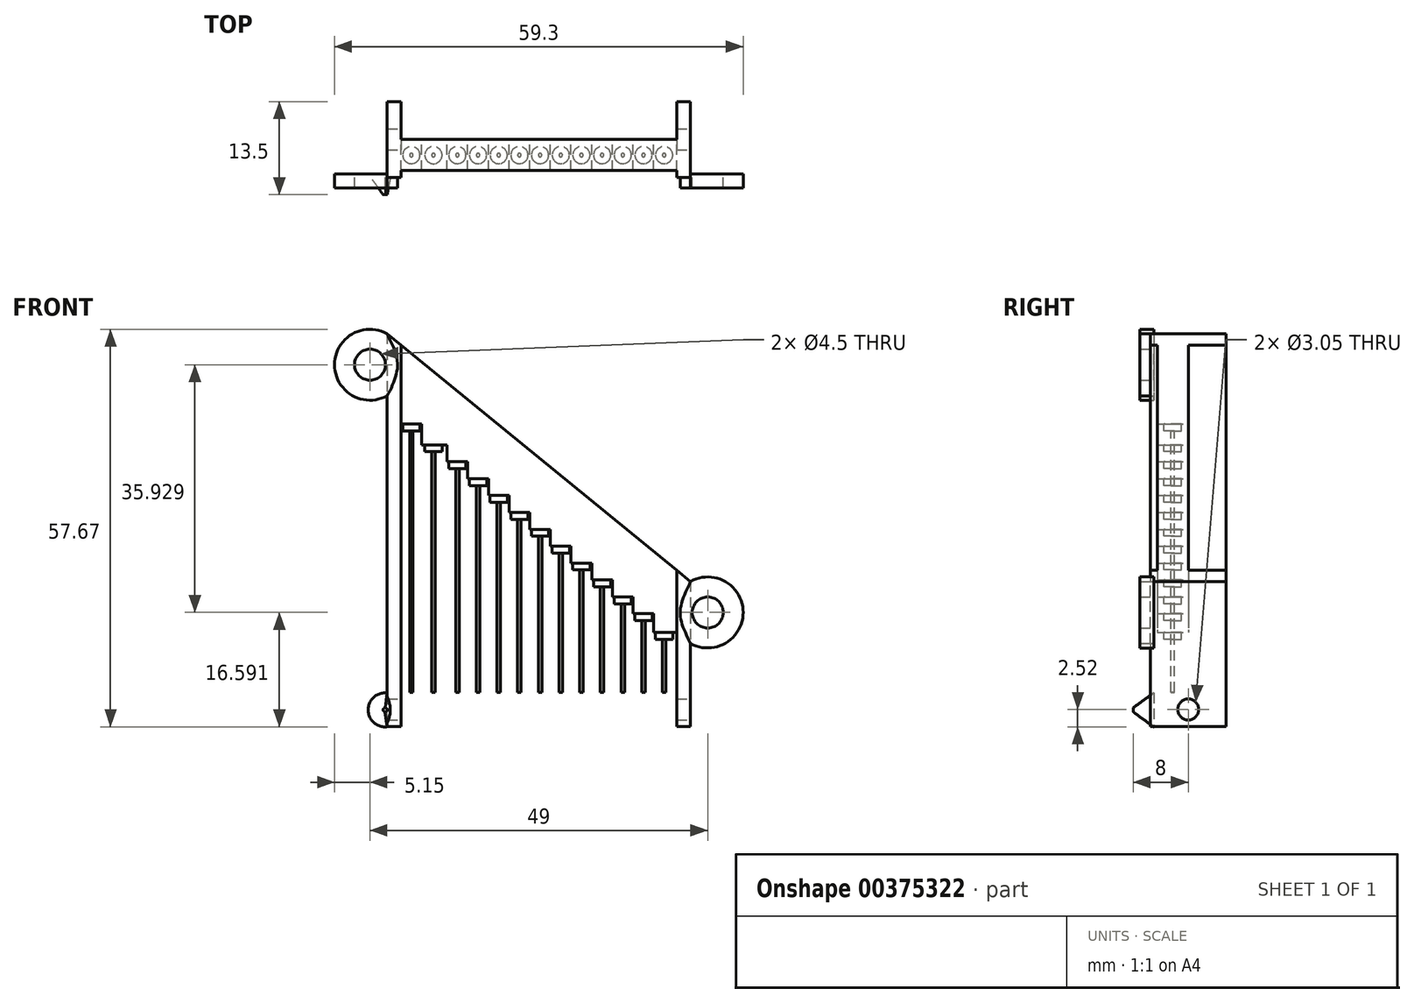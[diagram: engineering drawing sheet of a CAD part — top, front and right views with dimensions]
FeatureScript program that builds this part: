
annotation { "Feature Type Name" : "Feature", "Feature Type Description" : "" }
export const myFeature = defineFeature(function(context is Context, id is Id, definition is map)
    precondition{}
    {
        {
            var Q0;
            Q0=qCreatedBy(makeId("Front.planeOp"),FACE);
            var sketch = newSketch(context, id + "F0", { "sketchPlane" : qUnion([Q0])});
            skLineSegment(sketch, "E0.top", {"start": v(-22, -28.5) * mm, "end": v(22, -28.5) * mm});
            skLineSegment(sketch, "E0.left", {"start": v(-22, 28.5) * mm, "end": v(-22, -28.5) * mm});
            skPoint(sketch, "E0.middle", {"position": v(0, 0) * mm});
            skLineSegment(sketch, "E1", {"start": v(-22, 28.5) * mm, "end": v(22, -7.43) * mm});
            skPoint(sketch, "E2.orphan", {"position": v(22, 28.5) * mm});
            skLineSegment(sketch, "E3", {"start": v(22, -7.43) * mm, "end": v(22, -28.5) * mm});
            skLineSegment(sketch, "E4", {"start": v(22, -7.43) * mm, "end": v(-22, 28.5) * mm});
            skLineSegment(sketch, "E5", {"start": v(-20, -28.5) * mm, "end": v(-20, 26.87) * mm});
            skLineSegment(sketch, "E6", {"start": v(20, -5.8) * mm, "end": v(20, -28.5) * mm});
            skLineSegment(sketch, "E7", {"start": v(16.67, -12.12) * mm, "end": v(20, -14.83) * mm});
            skLineSegment(sketch, "E8", {"start": v(-20, 15.38) * mm, "end": v(-17, 15.38) * mm});
            skLineSegment(sketch, "E9", {"start": v(-17, 15.38) * mm, "end": v(-17, 12.38) * mm});
            skLineSegment(sketch, "E10", {"start": v(-17, 12.38) * mm, "end": v(-13.33, 12.38) * mm});
            skLineSegment(sketch, "E11", {"start": v(-13.33, 12.38) * mm, "end": v(-13.33, 9.93) * mm});
            skLineSegment(sketch, "E12", {"start": v(-13.33, 9.93) * mm, "end": v(-10.33, 9.93) * mm});
            skLineSegment(sketch, "E13", {"start": v(-10.33, 9.93) * mm, "end": v(-10.33, 7.48) * mm});
            skLineSegment(sketch, "E14", {"start": v(-10.33, 7.48) * mm, "end": v(-7.33, 7.48) * mm});
            skLineSegment(sketch, "E15", {"start": v(-7.33, 7.48) * mm, "end": v(-7.33, 5.03) * mm});
            skLineSegment(sketch, "E16", {"start": v(-7.33, 5.03) * mm, "end": v(-4.33, 5.03) * mm});
            skLineSegment(sketch, "E17", {"start": v(-4.33, 5.03) * mm, "end": v(-4.33, 2.58) * mm});
            skLineSegment(sketch, "E18", {"start": v(-4.33, 2.58) * mm, "end": v(-1.33, 2.58) * mm});
            skLineSegment(sketch, "E19", {"start": v(-1.33, 2.58) * mm, "end": v(-1.33, 0.13) * mm});
            skLineSegment(sketch, "E20", {"start": v(-1.33, 0.13) * mm, "end": v(1.67, 0.13) * mm});
            skLineSegment(sketch, "E21", {"start": v(1.67, 0.13) * mm, "end": v(1.67, -2.32) * mm});
            skLineSegment(sketch, "E22", {"start": v(1.67, -2.32) * mm, "end": v(4.67, -2.32) * mm});
            skLineSegment(sketch, "E23", {"start": v(4.67, -2.32) * mm, "end": v(4.67, -4.77) * mm});
            skLineSegment(sketch, "E24", {"start": v(4.67, -4.77) * mm, "end": v(7.67, -4.77) * mm});
            skLineSegment(sketch, "E25", {"start": v(7.67, -4.77) * mm, "end": v(7.67, -7.22) * mm});
            skLineSegment(sketch, "E26", {"start": v(7.67, -7.22) * mm, "end": v(10.67, -7.22) * mm});
            skLineSegment(sketch, "E27", {"start": v(10.67, -7.22) * mm, "end": v(10.67, -9.67) * mm});
            skLineSegment(sketch, "E28", {"start": v(10.67, -9.67) * mm, "end": v(13.67, -9.67) * mm});
            skLineSegment(sketch, "E29", {"start": v(13.67, -9.67) * mm, "end": v(13.67, -12.12) * mm});
            skLineSegment(sketch, "E30", {"start": v(13.67, -12.12) * mm, "end": v(16.67, -12.12) * mm});
            skLineSegment(sketch, "E31", {"start": v(16.67, -12.12) * mm, "end": v(16.67, -14.83) * mm});
            skLineSegment(sketch, "E32", {"start": v(16.67, -14.83) * mm, "end": v(20, -14.83) * mm});
            skSolve(sketch);
        }
        {
            var Q0;
            {var subQ0=sQuery(id+"F0.wireOp",EDGE,"E7");Q0=makeQuery(id+"F0.imprint","IMPRINT",FACE,{"disambiguationData":[TD([[makeQuery(id+"F0.imprint","IMPRINT",EDGE,{"derivedFrom":subQ0}),1.0]])]});}
            var Q1;
            Q1=makeQuery(id+"F0.imprint","IMPRINT",FACE,{"disambiguationData":[TD([[makeQuery(id+"F0.imprint","IMPRINT",EDGE,{"derivedFrom":sQuery(id+"F0.wireOp",EDGE,"E7")}),-1.0]])]});
            extrude(context, id + "F1", {"entities" : qUnion([Q0, Q1]), "depth" : 4.5 * mm});
        }
        {
            var Q0;
            {var subQ0=sQuery(id+"F0.wireOp",EDGE,"E0.left");Q0=makeQuery(id+"F0.imprint","IMPRINT",FACE,{"disambiguationData":[TD([[makeQuery(id+"F0.imprint","IMPRINT",EDGE,{"derivedFrom":subQ0}),1.0]])]});}
            var Q1;
            {var subQ0=sQuery(id+"F0.wireOp",EDGE,"E3");Q1=makeQuery(id+"F0.imprint","IMPRINT",FACE,{"disambiguationData":[TD([[makeQuery(id+"F0.imprint","IMPRINT",EDGE,{"derivedFrom":subQ0}),-1.0]])]});}
            extrude(context, id + "F2", {"entities" : qUnion([Q0, Q1]), "operationType" : NewBodyOperationType.ADD, "endBound" : BoundingType.SYMMETRIC, "depth" : 11 * mm});
        }
        {
            var Q0;
            Q0=makeQuery(id+"F1.opExtrude","SWEPT_FACE",FACE,{"disambiguationData":[OSD([sQuery(id+"F0.wireOp",EDGE,"E8")])]});
            var sketch = newSketch(context, id + "F3", { "sketchPlane" : qUnion([Q0])});
            skCircle(sketch, "E33", {"center": v(-18.5, 2.25) * mm, "radius": 1.25 * mm});
            skSolve(sketch);
        }
        {
            var Q0;
            Q0=makeQuery(id+"F1.opExtrude","SWEPT_FACE",FACE,{"disambiguationData":[OSD([sQuery(id+"F0.wireOp",EDGE,"E10")])]});
            var sketch = newSketch(context, id + "F4", { "sketchPlane" : qUnion([Q0])});
            skCircle(sketch, "E34", {"center": v(-15.3, 2.25) * mm, "radius": 1.25 * mm});
            skSolve(sketch);
        }
        {
            var Q0;
            Q0=makeQuery(id+"F1.opExtrude","SWEPT_FACE",FACE,{"disambiguationData":[OSD([sQuery(id+"F0.wireOp",EDGE,"E12")])]});
            var sketch = newSketch(context, id + "F5", { "sketchPlane" : qUnion([Q0])});
            skCircle(sketch, "E35", {"center": v(-11.83, 2.25) * mm, "radius": 1.25 * mm});
            skSolve(sketch);
        }
        {
            var Q0;
            Q0=makeQuery(id+"F1.opExtrude","SWEPT_FACE",FACE,{"disambiguationData":[OSD([sQuery(id+"F0.wireOp",EDGE,"E14")])]});
            var sketch = newSketch(context, id + "F6", { "sketchPlane" : qUnion([Q0])});
            skCircle(sketch, "E36", {"center": v(-8.83, 2.25) * mm, "radius": 1.25 * mm});
            skSolve(sketch);
        }
        {
            var Q0;
            Q0=makeQuery(id+"F1.opExtrude","SWEPT_FACE",FACE,{"disambiguationData":[OSD([sQuery(id+"F0.wireOp",EDGE,"E16")])]});
            var sketch = newSketch(context, id + "F7", { "sketchPlane" : qUnion([Q0])});
            skCircle(sketch, "E37", {"center": v(-5.83, 2.25) * mm, "radius": 1.25 * mm});
            skSolve(sketch);
        }
        {
            var Q0;
            Q0=makeQuery(id+"F1.opExtrude","SWEPT_FACE",FACE,{"disambiguationData":[OSD([sQuery(id+"F0.wireOp",EDGE,"E18")])]});
            var sketch = newSketch(context, id + "F8", { "sketchPlane" : qUnion([Q0])});
            skCircle(sketch, "E38", {"center": v(-2.83, 2.25) * mm, "radius": 1.25 * mm});
            skSolve(sketch);
        }
        {
            var Q0;
            Q0=makeQuery(id+"F1.opExtrude","SWEPT_FACE",FACE,{"disambiguationData":[OSD([sQuery(id+"F0.wireOp",EDGE,"E20")])]});
            var sketch = newSketch(context, id + "F9", { "sketchPlane" : qUnion([Q0])});
            skCircle(sketch, "E39", {"center": v(0.17, 2.25) * mm, "radius": 1.25 * mm});
            skCircle(sketch, "E40", {"center": v(0.17, 2.25) * mm, "radius": 0.2 * mm});
            skSolve(sketch);
        }
        {
            var Q0;
            Q0=makeQuery(id+"F1.opExtrude","SWEPT_FACE",FACE,{"disambiguationData":[OSD([sQuery(id+"F0.wireOp",EDGE,"E22")])]});
            var sketch = newSketch(context, id + "F10", { "sketchPlane" : qUnion([Q0])});
            skCircle(sketch, "E41", {"center": v(3.17, 2.25) * mm, "radius": 1.25 * mm});
            skSolve(sketch);
        }
        {
            var Q0;
            Q0=makeQuery(id+"F1.opExtrude","SWEPT_FACE",FACE,{"disambiguationData":[OSD([sQuery(id+"F0.wireOp",EDGE,"E24")])]});
            var sketch = newSketch(context, id + "F11", { "sketchPlane" : qUnion([Q0])});
            skCircle(sketch, "E42", {"center": v(6.17, 2.25) * mm, "radius": 1.25 * mm});
            skSolve(sketch);
        }
        {
            var Q0;
            Q0=makeQuery(id+"F1.opExtrude","SWEPT_FACE",FACE,{"disambiguationData":[OSD([sQuery(id+"F0.wireOp",EDGE,"E26")])]});
            var sketch = newSketch(context, id + "F12", { "sketchPlane" : qUnion([Q0])});
            skCircle(sketch, "E43", {"center": v(9.17, 2.25) * mm, "radius": 1.25 * mm});
            skSolve(sketch);
        }
        {
            var Q0;
            Q0=makeQuery(id+"F1.opExtrude","SWEPT_FACE",FACE,{"disambiguationData":[OSD([sQuery(id+"F0.wireOp",EDGE,"E28")])]});
            var sketch = newSketch(context, id + "F13", { "sketchPlane" : qUnion([Q0])});
            skCircle(sketch, "E44", {"center": v(12.17, 2.25) * mm, "radius": 1.25 * mm});
            skSolve(sketch);
        }
        {
            var Q0;
            Q0=makeQuery(id+"F1.opExtrude","SWEPT_FACE",FACE,{"disambiguationData":[OSD([sQuery(id+"F0.wireOp",EDGE,"E30")])]});
            var sketch = newSketch(context, id + "F14", { "sketchPlane" : qUnion([Q0])});
            skCircle(sketch, "E45", {"center": v(15.17, 2.25) * mm, "radius": 1.25 * mm});
            skSolve(sketch);
        }
        {
            var Q0;
            Q0=makeQuery(id+"F1.opExtrude","SWEPT_FACE",FACE,{"disambiguationData":[OSD([sQuery(id+"F0.wireOp",EDGE,"E32")])]});
            var sketch = newSketch(context, id + "F15", { "sketchPlane" : qUnion([Q0])});
            skCircle(sketch, "E46", {"center": v(18.17, 2.25) * mm, "radius": 1.25 * mm});
            skSolve(sketch);
        }
        {
            var Q0;
            Q0=makeQuery(id+"F3.imprint","IMPRINT",FACE,{"disambiguationData":[TD([[makeQuery(id+"F3.imprint","IMPRINT",EDGE,{"derivedFrom":sQuery(id+"F3.wireOp",EDGE,"E33")}),1.0]])]});
            var Q1;
            Q1=makeQuery(id+"F4.imprint","IMPRINT",FACE,{"disambiguationData":[TD([[makeQuery(id+"F4.imprint","IMPRINT",EDGE,{"derivedFrom":sQuery(id+"F4.wireOp",EDGE,"E34")}),1.0]])]});
            var Q2;
            Q2=makeQuery(id+"F5.imprint","IMPRINT",FACE,{"disambiguationData":[TD([[makeQuery(id+"F5.imprint","IMPRINT",EDGE,{"derivedFrom":sQuery(id+"F5.wireOp",EDGE,"E35")}),1.0]])]});
            var Q3;
            Q3=makeQuery(id+"F6.imprint","IMPRINT",FACE,{"disambiguationData":[TD([[makeQuery(id+"F6.imprint","IMPRINT",EDGE,{"derivedFrom":sQuery(id+"F6.wireOp",EDGE,"E36")}),1.0]])]});
            var Q4;
            Q4=makeQuery(id+"F7.imprint","IMPRINT",FACE,{"disambiguationData":[TD([[makeQuery(id+"F7.imprint","IMPRINT",EDGE,{"derivedFrom":sQuery(id+"F7.wireOp",EDGE,"E37")}),1.0]])]});
            var Q5;
            Q5=makeQuery(id+"F8.imprint","IMPRINT",FACE,{"disambiguationData":[TD([[makeQuery(id+"F8.imprint","IMPRINT",EDGE,{"derivedFrom":sQuery(id+"F8.wireOp",EDGE,"E38")}),1.0]])]});
            var Q6;
            Q6=makeQuery(id+"F9.imprint","IMPRINT",FACE,{"disambiguationData":[TD([[makeQuery(id+"F9.imprint","IMPRINT",EDGE,{"derivedFrom":sQuery(id+"F9.wireOp",EDGE,"E39")}),1.0]])]});
            var Q7;
            Q7=makeQuery(id+"F9.imprint","IMPRINT",FACE,{"disambiguationData":[TD([[makeQuery(id+"F9.imprint","IMPRINT",EDGE,{"derivedFrom":sQuery(id+"F9.wireOp",EDGE,"E40")}),1.0]])]});
            var Q8;
            Q8=makeQuery(id+"F10.imprint","IMPRINT",FACE,{"disambiguationData":[TD([[makeQuery(id+"F10.imprint","IMPRINT",EDGE,{"derivedFrom":sQuery(id+"F10.wireOp",EDGE,"E41")}),1.0]])]});
            var Q9;
            Q9=makeQuery(id+"F11.imprint","IMPRINT",FACE,{"disambiguationData":[TD([[makeQuery(id+"F11.imprint","IMPRINT",EDGE,{"derivedFrom":sQuery(id+"F11.wireOp",EDGE,"E42")}),1.0]])]});
            var Q10;
            Q10=makeQuery(id+"F12.imprint","IMPRINT",FACE,{"disambiguationData":[TD([[makeQuery(id+"F12.imprint","IMPRINT",EDGE,{"derivedFrom":sQuery(id+"F12.wireOp",EDGE,"E43")}),1.0]])]});
            var Q11;
            Q11=makeQuery(id+"F13.imprint","IMPRINT",FACE,{"disambiguationData":[TD([[makeQuery(id+"F13.imprint","IMPRINT",EDGE,{"derivedFrom":sQuery(id+"F13.wireOp",EDGE,"E44")}),1.0]])]});
            var Q12;
            Q12=makeQuery(id+"F14.imprint","IMPRINT",FACE,{"disambiguationData":[TD([[makeQuery(id+"F14.imprint","IMPRINT",EDGE,{"derivedFrom":sQuery(id+"F14.wireOp",EDGE,"E45")}),1.0]])]});
            var Q13;
            Q13=makeQuery(id+"F15.imprint","IMPRINT",FACE,{"disambiguationData":[TD([[makeQuery(id+"F15.imprint","IMPRINT",EDGE,{"derivedFrom":sQuery(id+"F15.wireOp",EDGE,"E46")}),1.0]])]});
            extrude(context, id + "F16", {"entities" : qUnion([Q0, Q1, Q2, Q3, Q4, Q5, Q6, Q7, Q8, Q9, Q10, Q11, Q12, Q13]), "operationType" : NewBodyOperationType.ADD, "depth" : 1 * mm});
        }
        {
            var Q0;
            Q0=makeQuery(id+"F16.opExtrude","CAP_FACE",FACE,{"disambiguationData":[OSD([sQuery(id+"F3.wireOp",EDGE,"E33")])],"isStart":false});
            var sketch = newSketch(context, id + "F17", { "sketchPlane" : qUnion([Q0])});
            skCircle(sketch, "E47", {"center": v(-18.5, 2.25) * mm, "radius": 0.25 * mm});
            skSolve(sketch);
        }
        {
            var Q0;
            Q0=makeQuery(id+"F16.opExtrude","CAP_FACE",FACE,{"disambiguationData":[OSD([sQuery(id+"F4.wireOp",EDGE,"E34")])],"isStart":false});
            var sketch = newSketch(context, id + "F18", { "sketchPlane" : qUnion([Q0])});
            skCircle(sketch, "E48", {"center": v(-15.3, 2.25) * mm, "radius": 0.25 * mm});
            skSolve(sketch);
        }
        {
            var Q0;
            Q0=makeQuery(id+"F16.opExtrude","CAP_FACE",FACE,{"disambiguationData":[OSD([sQuery(id+"F5.wireOp",EDGE,"E35")])],"isStart":false});
            var sketch = newSketch(context, id + "F19", { "sketchPlane" : qUnion([Q0])});
            skCircle(sketch, "E49", {"center": v(-11.83, 2.25) * mm, "radius": 0.25 * mm});
            skSolve(sketch);
        }
        {
            var Q0;
            Q0=makeQuery(id+"F16.opExtrude","CAP_FACE",FACE,{"disambiguationData":[OSD([sQuery(id+"F6.wireOp",EDGE,"E36")])],"isStart":false});
            var sketch = newSketch(context, id + "F20", { "sketchPlane" : qUnion([Q0])});
            skCircle(sketch, "E50", {"center": v(-8.83, 2.25) * mm, "radius": 0.25 * mm});
            skSolve(sketch);
        }
        {
            var Q0;
            Q0=makeQuery(id+"F16.opExtrude","CAP_FACE",FACE,{"disambiguationData":[OSD([sQuery(id+"F7.wireOp",EDGE,"E37")])],"isStart":false});
            var sketch = newSketch(context, id + "F21", { "sketchPlane" : qUnion([Q0])});
            skCircle(sketch, "E51", {"center": v(-5.83, 2.25) * mm, "radius": 0.25 * mm});
            skSolve(sketch);
        }
        {
            var Q0;
            Q0=makeQuery(id+"F16.opExtrude","CAP_FACE",FACE,{"disambiguationData":[OSD([sQuery(id+"F8.wireOp",EDGE,"E38")])],"isStart":false});
            var sketch = newSketch(context, id + "F22", { "sketchPlane" : qUnion([Q0])});
            skCircle(sketch, "E52", {"center": v(-2.83, 2.25) * mm, "radius": 0.25 * mm});
            skSolve(sketch);
        }
        {
            var Q0;
            Q0=makeQuery(id+"F16.opExtrude","CAP_FACE",FACE,{"disambiguationData":[OSD([sQuery(id+"F9.wireOp",EDGE,"E39")])],"isStart":false});
            var sketch = newSketch(context, id + "F23", { "sketchPlane" : qUnion([Q0])});
            skCircle(sketch, "E53", {"center": v(0.17, 2.25) * mm, "radius": 0.25 * mm});
            skSolve(sketch);
        }
        {
            var Q0;
            Q0=makeQuery(id+"F16.opExtrude","CAP_FACE",FACE,{"disambiguationData":[OSD([sQuery(id+"F10.wireOp",EDGE,"E41")])],"isStart":false});
            var sketch = newSketch(context, id + "F24", { "sketchPlane" : qUnion([Q0])});
            skCircle(sketch, "E54", {"center": v(3.17, 2.25) * mm, "radius": 0.25 * mm});
            skSolve(sketch);
        }
        {
            var Q0;
            Q0=makeQuery(id+"F16.opExtrude","CAP_FACE",FACE,{"disambiguationData":[OSD([sQuery(id+"F11.wireOp",EDGE,"E42")])],"isStart":false});
            var sketch = newSketch(context, id + "F25", { "sketchPlane" : qUnion([Q0])});
            skCircle(sketch, "E55", {"center": v(6.17, 2.25) * mm, "radius": 0.25 * mm});
            skSolve(sketch);
        }
        {
            var Q0;
            Q0=makeQuery(id+"F16.opExtrude","CAP_FACE",FACE,{"disambiguationData":[OSD([sQuery(id+"F12.wireOp",EDGE,"E43")])],"isStart":false});
            var sketch = newSketch(context, id + "F26", { "sketchPlane" : qUnion([Q0])});
            skCircle(sketch, "E56", {"center": v(9.17, 2.25) * mm, "radius": 0.25 * mm});
            skSolve(sketch);
        }
        {
            var Q0;
            Q0=makeQuery(id+"F16.opExtrude","CAP_FACE",FACE,{"disambiguationData":[OSD([sQuery(id+"F13.wireOp",EDGE,"E44")])],"isStart":false});
            var sketch = newSketch(context, id + "F27", { "sketchPlane" : qUnion([Q0])});
            skCircle(sketch, "E57", {"center": v(12.17, 2.25) * mm, "radius": 0.25 * mm});
            skSolve(sketch);
        }
        {
            var Q0;
            Q0=makeQuery(id+"F16.opExtrude","CAP_FACE",FACE,{"disambiguationData":[OSD([sQuery(id+"F14.wireOp",EDGE,"E45")])],"isStart":false});
            var sketch = newSketch(context, id + "F28", { "sketchPlane" : qUnion([Q0])});
            skCircle(sketch, "E58", {"center": v(15.17, 2.25) * mm, "radius": 0.25 * mm});
            skSolve(sketch);
        }
        {
            var Q0;
            Q0=makeQuery(id+"F16.opExtrude","CAP_FACE",FACE,{"disambiguationData":[OSD([sQuery(id+"F15.wireOp",EDGE,"E46")])],"isStart":false});
            var sketch = newSketch(context, id + "F29", { "sketchPlane" : qUnion([Q0])});
            skCircle(sketch, "E59", {"center": v(18.17, 2.25) * mm, "radius": 0.25 * mm});
            skSolve(sketch);
        }
        {
            var Q0;
            {var subQ0=sQuery(id+"F0.wireOp",EDGE,"E0.top");Q0=makeQuery(id+"F2.opExtrude","SWEPT_FACE",FACE,{"disambiguationData":[OSD([subQ0]),TDD([makeQuery(id+"F0.imprint","IMPRINT",EDGE,{"disambiguationData":[TD([[makeQuery(id+"F0.imprint","INTERSECT",VERTEX,{"derivedFrom":[subQ0,sQuery(id+"F0.wireOp",EDGE,"E3")]}),1.0]])],"derivedFrom":subQ0})])]});}
            cPlane(context, id + "F30", {"entities" : qUnion([Q0]), "cplaneType" : CPlaneType.OFFSET, "offset" : 5 * mm, "oppositeDirection" : true, "width" : 150 * mm, "height" : 150 * mm});
        }
        {
            var Q0;
            Q0=makeQuery(id+"F29.imprint","IMPRINT",FACE,{"disambiguationData":[TD([[makeQuery(id+"F29.imprint","IMPRINT",EDGE,{"derivedFrom":sQuery(id+"F29.wireOp",EDGE,"E59")}),1.0]])]});
            var Q1;
            Q1=makeQuery(id+"F28.imprint","IMPRINT",FACE,{"disambiguationData":[TD([[makeQuery(id+"F28.imprint","IMPRINT",EDGE,{"derivedFrom":sQuery(id+"F28.wireOp",EDGE,"E58")}),1.0]])]});
            var Q2;
            Q2=makeQuery(id+"F27.imprint","IMPRINT",FACE,{"disambiguationData":[TD([[makeQuery(id+"F27.imprint","IMPRINT",EDGE,{"derivedFrom":sQuery(id+"F27.wireOp",EDGE,"E57")}),1.0]])]});
            var Q3;
            Q3=makeQuery(id+"F26.imprint","IMPRINT",FACE,{"disambiguationData":[TD([[makeQuery(id+"F26.imprint","IMPRINT",EDGE,{"derivedFrom":sQuery(id+"F26.wireOp",EDGE,"E56")}),1.0]])]});
            var Q4;
            Q4=makeQuery(id+"F25.imprint","IMPRINT",FACE,{"disambiguationData":[TD([[makeQuery(id+"F25.imprint","IMPRINT",EDGE,{"derivedFrom":sQuery(id+"F25.wireOp",EDGE,"E55")}),1.0]])]});
            var Q5;
            Q5=makeQuery(id+"F24.imprint","IMPRINT",FACE,{"disambiguationData":[TD([[makeQuery(id+"F24.imprint","IMPRINT",EDGE,{"derivedFrom":sQuery(id+"F24.wireOp",EDGE,"E54")}),1.0]])]});
            var Q6;
            Q6=makeQuery(id+"F23.imprint","IMPRINT",FACE,{"disambiguationData":[TD([[makeQuery(id+"F23.imprint","IMPRINT",EDGE,{"derivedFrom":sQuery(id+"F23.wireOp",EDGE,"E53")}),1.0]])]});
            var Q7;
            Q7=makeQuery(id+"F22.imprint","IMPRINT",FACE,{"disambiguationData":[TD([[makeQuery(id+"F22.imprint","IMPRINT",EDGE,{"derivedFrom":sQuery(id+"F22.wireOp",EDGE,"E52")}),1.0]])]});
            var Q8;
            Q8=makeQuery(id+"F21.imprint","IMPRINT",FACE,{"disambiguationData":[TD([[makeQuery(id+"F21.imprint","IMPRINT",EDGE,{"derivedFrom":sQuery(id+"F21.wireOp",EDGE,"E51")}),1.0]])]});
            var Q9;
            Q9=makeQuery(id+"F20.imprint","IMPRINT",FACE,{"disambiguationData":[TD([[makeQuery(id+"F20.imprint","IMPRINT",EDGE,{"derivedFrom":sQuery(id+"F20.wireOp",EDGE,"E50")}),1.0]])]});
            var Q10;
            Q10=makeQuery(id+"F19.imprint","IMPRINT",FACE,{"disambiguationData":[TD([[makeQuery(id+"F19.imprint","IMPRINT",EDGE,{"derivedFrom":sQuery(id+"F19.wireOp",EDGE,"E49")}),1.0]])]});
            var Q11;
            Q11=makeQuery(id+"F18.imprint","IMPRINT",FACE,{"disambiguationData":[TD([[makeQuery(id+"F18.imprint","IMPRINT",EDGE,{"derivedFrom":sQuery(id+"F18.wireOp",EDGE,"E48")}),1.0]])]});
            var Q12;
            Q12=makeQuery(id+"F17.imprint","IMPRINT",FACE,{"disambiguationData":[TD([[makeQuery(id+"F17.imprint","IMPRINT",EDGE,{"derivedFrom":sQuery(id+"F17.wireOp",EDGE,"E47")}),1.0]])]});
            var Q13;
            Q13=qCreatedBy(id+"F30.planeOp",FACE);
            extrude(context, id + "F31", {"entities" : qUnion([Q0, Q1, Q2, Q3, Q4, Q5, Q6, Q7, Q8, Q9, Q10, Q11, Q12]), "operationType" : NewBodyOperationType.ADD, "endBound" : BoundingType.UP_TO_SURFACE, "endBoundEntityFace" : qUnion([Q13]), "depth" : 25 * mm});
        }
        {
            var Q0;
            Q0=makeQuery(id+"F2.opExtrude","SWEPT_FACE",FACE,{"disambiguationData":[OSD([sQuery(id+"F0.wireOp",EDGE,"E3")])]});
            var sketch = newSketch(context, id + "F32", { "sketchPlane" : qUnion([Q0])});
            skCircle(sketch, "E60", {"center": v(0, -26) * mm, "radius": 1.53 * mm});
            skSolve(sketch);
        }
        {
            var Q0;
            Q0=makeQuery(id+"F32.imprint","IMPRINT",FACE,{"disambiguationData":[TD([[makeQuery(id+"F32.imprint","IMPRINT",EDGE,{"derivedFrom":sQuery(id+"F32.wireOp",EDGE,"E60")}),1.0]])]});
            var Q1;
            Q1=makeQuery(id+"F2.opExtrude","SWEPT_FACE",FACE,{"disambiguationData":[OSD([sQuery(id+"F0.wireOp",EDGE,"E0.left")])]});
            extrude(context, id + "F33", {"entities" : qUnion([Q0]), "operationType" : NewBodyOperationType.REMOVE, "endBound" : BoundingType.UP_TO_SURFACE, "oppositeDirection" : true, "endBoundEntityFace" : qUnion([Q1]), "depth" : 25 * mm});
        }
        {
            var Q0;
            Q0=qCreatedBy(makeId("Front.planeOp"),FACE);
            cPlane(context, id + "F34", {"entities" : qUnion([Q0]), "cplaneType" : CPlaneType.OFFSET, "offset" : 5 * mm, "width" : 150 * mm, "height" : 150 * mm});
        }
        {
            var Q0;
            Q0=qCreatedBy(id+"F34.planeOp",FACE);
            var sketch = newSketch(context, id + "F35", { "sketchPlane" : qUnion([Q0])});
            skArc(sketch, "E61", {"start": v(-22, 28.5) * mm, "mid": v(-29.65, 24) * mm, "end": v(-22, 19.5) * mm});
            skCircle(sketch, "E62", {"center": v(-24.5, 24) * mm, "radius": 2.25 * mm});
            skLineSegment(sketch, "E63", {"start": v(-22, 28.5) * mm, "end": v(-22, 19.5) * mm});
            skFitSpline(sketch, "E64", {"points": [v(-22, 28.5) * mm, v(-20.5, 24) * mm, v(-22, 19.5) * mm], "startDerivative": vector(4.44, -9.43) * mm, "endDerivative": vector(-4.52, -8.57) * mm});
            skSolve(sketch);
        }
        {
            var Q0;
            Q0=makeQuery(id+"F35.imprint","IMPRINT",FACE,{"disambiguationData":[TD([[makeQuery(id+"F35.imprint","IMPRINT",EDGE,{"derivedFrom":sQuery(id+"F35.wireOp",EDGE,"E61")}),1.0]])]});
            var Q1;
            Q1=makeQuery(id+"F35.imprint","IMPRINT",FACE,{"disambiguationData":[TD([[makeQuery(id+"F35.imprint","IMPRINT",EDGE,{"derivedFrom":sQuery(id+"F35.wireOp",EDGE,"E63")}),1.0]])]});
            extrude(context, id + "F36", {"entities" : qUnion([Q0, Q1]), "operationType" : NewBodyOperationType.ADD, "depth" : 2 * mm});
        }
        {
            var Q0;
            Q0=qCreatedBy(id+"F34.planeOp",FACE);
            var sketch = newSketch(context, id + "F37", { "sketchPlane" : qUnion([Q0])});
            skArc(sketch, "E65", {"start": v(22, -16.43) * mm, "mid": v(29.65, -11.93) * mm, "end": v(22, -7.43) * mm});
            skCircle(sketch, "E66", {"center": v(24.5, -11.93) * mm, "radius": 2.25 * mm});
            skLineSegment(sketch, "E67", {"start": v(22, -16.43) * mm, "end": v(22, -7.43) * mm});
            skFitSpline(sketch, "E68", {"points": [v(22, -16.43) * mm, v(20.5, -11.93) * mm, v(22, -7.43) * mm], "startDerivative": vector(-4.44, 9.43) * mm, "endDerivative": vector(3.96, 8.57) * mm});
            skSolve(sketch);
        }
        {
            var Q0;
            Q0=makeQuery(id+"F37.imprint","IMPRINT",FACE,{"disambiguationData":[TD([[makeQuery(id+"F37.imprint","IMPRINT",EDGE,{"derivedFrom":sQuery(id+"F37.wireOp",EDGE,"E65")}),1.0]])]});
            var Q1;
            Q1=makeQuery(id+"F37.imprint","IMPRINT",FACE,{"disambiguationData":[TD([[makeQuery(id+"F37.imprint","IMPRINT",EDGE,{"derivedFrom":sQuery(id+"F37.wireOp",EDGE,"E67")}),1.0]])]});
            extrude(context, id + "F38", {"entities" : qUnion([Q0, Q1]), "operationType" : NewBodyOperationType.ADD, "depth" : 2 * mm});
        }
        {
            var Q0;
            Q0=qCreatedBy(id+"F34.planeOp",FACE);
            var sketch = newSketch(context, id + "F39", { "sketchPlane" : qUnion([Q0])});
            skArc(sketch, "E69", {"start": v(-22, -23.6) * mm, "mid": v(-24.76, -26.05) * mm, "end": v(-22, -28.5) * mm});
            skLineSegment(sketch, "E70", {"start": v(-22, -23.6) * mm, "end": v(-22, -28.5) * mm});
            skFitSpline(sketch, "E71", {"points": [v(-22, -23.6) * mm, v(-21.47, -26.14) * mm, v(-22, -28.5) * mm], "startDerivative": vector(1.5, -5.06) * mm, "endDerivative": vector(-1.51, -4.78) * mm});
            skSolve(sketch);
        }
        {
            var Q0;
            Q0=qCreatedBy(id+"F34.planeOp",FACE);
            cPlane(context, id + "F40", {"entities" : qUnion([Q0]), "cplaneType" : CPlaneType.OFFSET, "offset" : 3 * mm, "width" : 150 * mm, "height" : 150 * mm});
        }
        {
            var Q0;
            Q0=qCreatedBy(id+"F40.planeOp",FACE);
            var sketch = newSketch(context, id + "F41", { "sketchPlane" : qUnion([Q0])});
            skCircle(sketch, "E72", {"center": v(-22.3, -26.05) * mm, "radius": 0.3 * mm});
            skSolve(sketch);
        }
        {
            var Q0;
            Q0 = qSketchRegion(id + "F39", true);
            var Q1;
            Q1 = qSketchRegion(id + "F41", true);
            loft(context, id + "F42", {"operationType" : NewBodyOperationType.ADD, "sheetProfilesArray" : [{ "sheetProfileEntities" : qUnion([Q0]) }, { "sheetProfileEntities" : qUnion([Q1]) }]});
        }
    });
